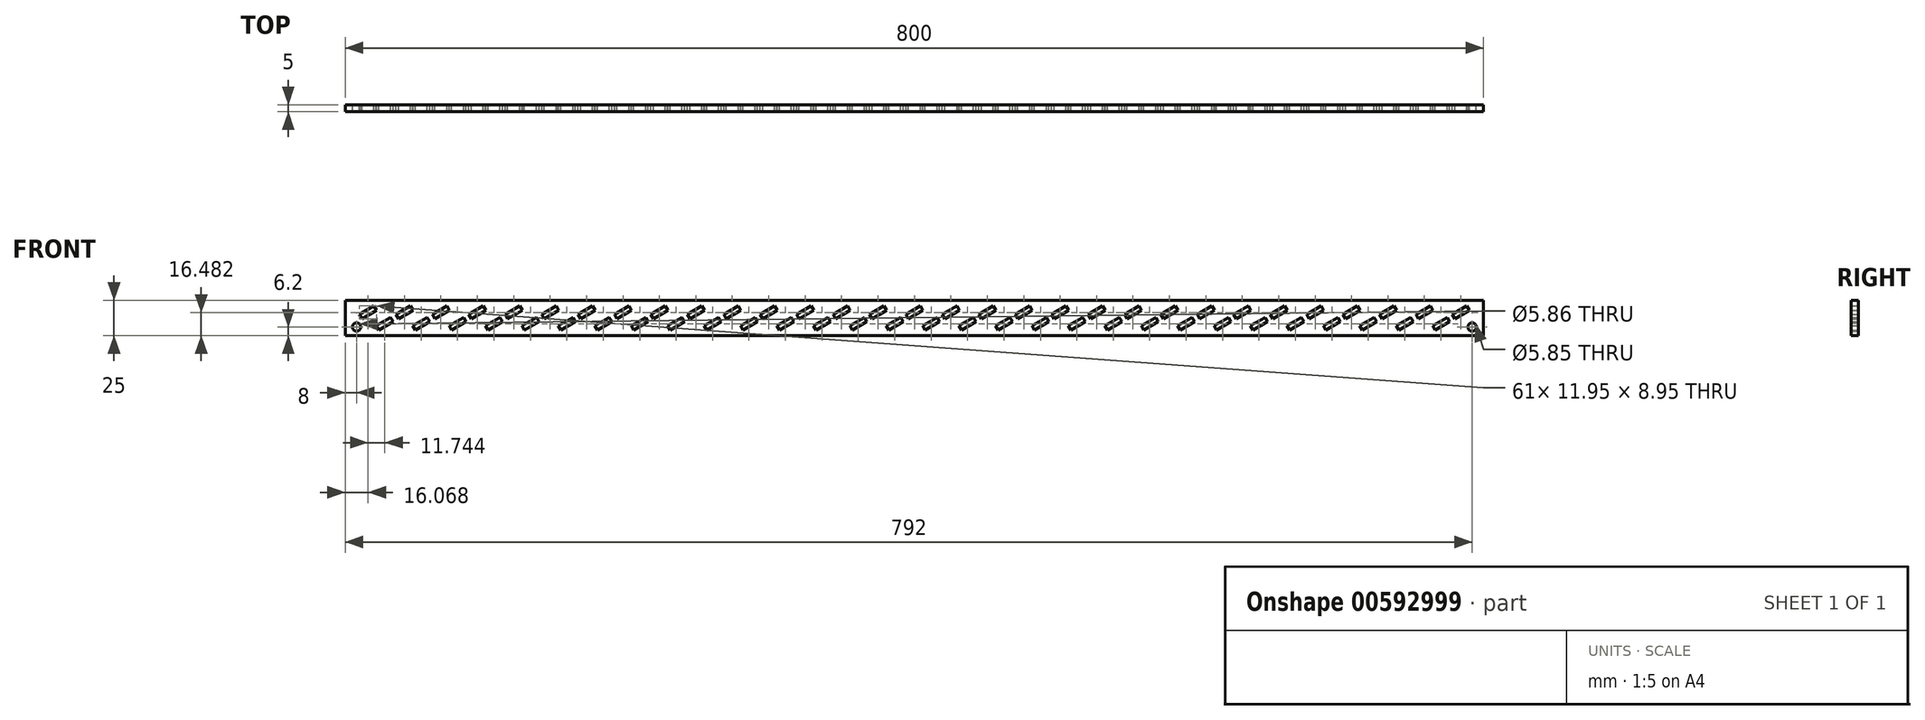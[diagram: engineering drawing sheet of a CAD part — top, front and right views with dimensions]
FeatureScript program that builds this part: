
annotation { "Feature Type Name" : "Feature", "Feature Type Description" : "" }
export const myFeature = defineFeature(function(context is Context, id is Id, definition is map)
    precondition{}
    {
        {
            var Q0;
            Q0=qCreatedBy(makeId("Front.planeOp"),FACE);
            var sketch = newSketch(context, id + "F0", { "sketchPlane" : qUnion([Q0])});
            skCircle(sketch, "E0", {"center": v(392, -6.3) * mm, "radius": 2.93 * mm});
            skCircle(sketch, "E1", {"center": v(192, 6.3) * mm, "radius": 2.93 * mm});
            skCircle(sketch, "E2", {"center": v(-1, -6.3) * mm, "radius": 2.93 * mm});
            skCircle(sketch, "E3", {"center": v(-216, 6.3) * mm, "radius": 2.93 * mm});
            skCircle(sketch, "E4", {"center": v(-392, -6.3) * mm, "radius": 2.93 * mm});
            skLineSegment(sketch, "E5", {"start": v(-382.04, 8.6) * mm, "end": v(-388.96, 4.6) * mm});
            skLineSegment(sketch, "E6", {"start": v(-385.96, -0.6) * mm, "end": v(-379.04, 3.4) * mm});
            skLineSegment(sketch, "E7", {"start": v(-370.3, 0.6) * mm, "end": v(-377.22, -3.4) * mm});
            skLineSegment(sketch, "E8", {"start": v(-374.22, -8.6) * mm, "end": v(-367.3, -4.6) * mm});
            skLineSegment(sketch, "E9", {"start": v(-356.44, 8.6) * mm, "end": v(-363.36, 4.6) * mm});
            skLineSegment(sketch, "E10", {"start": v(-360.36, -0.6) * mm, "end": v(-353.44, 3.4) * mm});
            skLineSegment(sketch, "E11", {"start": v(-344.7, 0.6) * mm, "end": v(-351.62, -3.4) * mm});
            skLineSegment(sketch, "E12", {"start": v(-348.62, -8.6) * mm, "end": v(-341.7, -4.6) * mm});
            skLineSegment(sketch, "E13", {"start": v(-330.84, 8.6) * mm, "end": v(-337.76, 4.6) * mm});
            skLineSegment(sketch, "E14", {"start": v(-334.76, -0.6) * mm, "end": v(-327.84, 3.4) * mm});
            skLineSegment(sketch, "E15", {"start": v(-319.1, 0.6) * mm, "end": v(-326.02, -3.4) * mm});
            skLineSegment(sketch, "E16", {"start": v(-323.02, -8.6) * mm, "end": v(-316.1, -4.6) * mm});
            skLineSegment(sketch, "E17", {"start": v(-305.24, 8.6) * mm, "end": v(-312.16, 4.6) * mm});
            skLineSegment(sketch, "E18", {"start": v(-309.16, -0.6) * mm, "end": v(-302.24, 3.4) * mm});
            skLineSegment(sketch, "E19", {"start": v(-293.5, 0.6) * mm, "end": v(-300.42, -3.4) * mm});
            skLineSegment(sketch, "E20", {"start": v(-297.42, -8.6) * mm, "end": v(-290.5, -4.6) * mm});
            skLineSegment(sketch, "E21", {"start": v(-279.64, 8.6) * mm, "end": v(-286.56, 4.6) * mm});
            skLineSegment(sketch, "E22", {"start": v(-283.56, -0.6) * mm, "end": v(-276.64, 3.4) * mm});
            skLineSegment(sketch, "E23", {"start": v(-267.9, 0.6) * mm, "end": v(-274.82, -3.4) * mm});
            skLineSegment(sketch, "E24", {"start": v(-271.82, -8.6) * mm, "end": v(-264.9, -4.6) * mm});
            skLineSegment(sketch, "E25", {"start": v(-254.04, 8.6) * mm, "end": v(-260.96, 4.6) * mm});
            skLineSegment(sketch, "E26", {"start": v(-257.96, -0.6) * mm, "end": v(-251.04, 3.4) * mm});
            skLineSegment(sketch, "E27", {"start": v(-242.3, 0.6) * mm, "end": v(-249.22, -3.4) * mm});
            skLineSegment(sketch, "E28", {"start": v(-246.22, -8.6) * mm, "end": v(-239.3, -4.6) * mm});
            skLineSegment(sketch, "E29", {"start": v(-228.44, 8.6) * mm, "end": v(-235.36, 4.6) * mm});
            skLineSegment(sketch, "E30", {"start": v(-232.36, -0.6) * mm, "end": v(-225.44, 3.4) * mm});
            skLineSegment(sketch, "E31", {"start": v(-216.7, 0.6) * mm, "end": v(-223.62, -3.4) * mm});
            skLineSegment(sketch, "E32", {"start": v(-220.62, -8.6) * mm, "end": v(-213.7, -4.6) * mm});
            skLineSegment(sketch, "E33", {"start": v(-202.84, 8.6) * mm, "end": v(-209.76, 4.6) * mm});
            skLineSegment(sketch, "E34", {"start": v(-206.76, -0.6) * mm, "end": v(-199.84, 3.4) * mm});
            skLineSegment(sketch, "E35", {"start": v(-191.1, 0.6) * mm, "end": v(-198.02, -3.4) * mm});
            skLineSegment(sketch, "E36", {"start": v(-195.02, -8.6) * mm, "end": v(-188.1, -4.6) * mm});
            skLineSegment(sketch, "E37", {"start": v(-177.24, 8.6) * mm, "end": v(-184.16, 4.6) * mm});
            skLineSegment(sketch, "E38", {"start": v(-181.16, -0.6) * mm, "end": v(-174.24, 3.4) * mm});
            skLineSegment(sketch, "E39", {"start": v(-165.5, 0.6) * mm, "end": v(-172.42, -3.4) * mm});
            skLineSegment(sketch, "E40", {"start": v(-169.42, -8.6) * mm, "end": v(-162.5, -4.6) * mm});
            skLineSegment(sketch, "E41", {"start": v(-151.64, 8.6) * mm, "end": v(-158.56, 4.6) * mm});
            skLineSegment(sketch, "E42", {"start": v(-155.56, -0.6) * mm, "end": v(-148.64, 3.4) * mm});
            skLineSegment(sketch, "E43", {"start": v(-139.9, 0.6) * mm, "end": v(-146.82, -3.4) * mm});
            skLineSegment(sketch, "E44", {"start": v(-143.82, -8.6) * mm, "end": v(-136.9, -4.6) * mm});
            skLineSegment(sketch, "E45", {"start": v(-126.04, 8.6) * mm, "end": v(-132.96, 4.6) * mm});
            skLineSegment(sketch, "E46", {"start": v(-129.96, -0.6) * mm, "end": v(-123.04, 3.4) * mm});
            skLineSegment(sketch, "E47", {"start": v(-114.3, 0.6) * mm, "end": v(-121.22, -3.4) * mm});
            skLineSegment(sketch, "E48", {"start": v(-118.22, -8.6) * mm, "end": v(-111.3, -4.6) * mm});
            skLineSegment(sketch, "E49", {"start": v(-100.44, 8.6) * mm, "end": v(-107.36, 4.6) * mm});
            skLineSegment(sketch, "E50", {"start": v(-104.36, -0.6) * mm, "end": v(-97.44, 3.4) * mm});
            skLineSegment(sketch, "E51", {"start": v(-88.7, 0.6) * mm, "end": v(-95.62, -3.4) * mm});
            skLineSegment(sketch, "E52", {"start": v(-92.62, -8.6) * mm, "end": v(-85.7, -4.6) * mm});
            skLineSegment(sketch, "E53", {"start": v(-74.84, 8.6) * mm, "end": v(-81.76, 4.6) * mm});
            skLineSegment(sketch, "E54", {"start": v(-78.76, -0.6) * mm, "end": v(-71.84, 3.4) * mm});
            skLineSegment(sketch, "E55", {"start": v(-63.1, 0.6) * mm, "end": v(-70.02, -3.4) * mm});
            skLineSegment(sketch, "E56", {"start": v(-67.02, -8.6) * mm, "end": v(-60.1, -4.6) * mm});
            skLineSegment(sketch, "E57", {"start": v(-49.24, 8.6) * mm, "end": v(-56.16, 4.6) * mm});
            skLineSegment(sketch, "E58", {"start": v(-53.16, -0.6) * mm, "end": v(-46.24, 3.4) * mm});
            skLineSegment(sketch, "E59", {"start": v(-37.5, 0.6) * mm, "end": v(-44.42, -3.4) * mm});
            skLineSegment(sketch, "E60", {"start": v(-41.42, -8.6) * mm, "end": v(-34.5, -4.6) * mm});
            skLineSegment(sketch, "E61", {"start": v(-23.64, 8.6) * mm, "end": v(-30.56, 4.6) * mm});
            skLineSegment(sketch, "E62", {"start": v(-27.56, -0.6) * mm, "end": v(-20.64, 3.4) * mm});
            skLineSegment(sketch, "E63", {"start": v(-11.9, 0.6) * mm, "end": v(-18.82, -3.4) * mm});
            skLineSegment(sketch, "E64", {"start": v(-15.82, -8.6) * mm, "end": v(-8.9, -4.6) * mm});
            skLineSegment(sketch, "E65", {"start": v(1.96, 8.6) * mm, "end": v(-4.96, 4.6) * mm});
            skLineSegment(sketch, "E66", {"start": v(-1.96, -0.6) * mm, "end": v(4.96, 3.4) * mm});
            skLineSegment(sketch, "E67", {"start": v(13.7, 0.6) * mm, "end": v(6.78, -3.4) * mm});
            skLineSegment(sketch, "E68", {"start": v(9.78, -8.6) * mm, "end": v(16.7, -4.6) * mm});
            skLineSegment(sketch, "E69", {"start": v(27.56, 8.6) * mm, "end": v(20.64, 4.6) * mm});
            skLineSegment(sketch, "E70", {"start": v(23.64, -0.6) * mm, "end": v(30.56, 3.4) * mm});
            skLineSegment(sketch, "E71", {"start": v(39.3, 0.6) * mm, "end": v(32.38, -3.4) * mm});
            skLineSegment(sketch, "E72", {"start": v(35.38, -8.6) * mm, "end": v(42.3, -4.6) * mm});
            skLineSegment(sketch, "E73", {"start": v(53.16, 8.6) * mm, "end": v(46.24, 4.6) * mm});
            skLineSegment(sketch, "E74", {"start": v(49.24, -0.6) * mm, "end": v(56.16, 3.4) * mm});
            skLineSegment(sketch, "E75", {"start": v(64.9, 0.6) * mm, "end": v(57.98, -3.4) * mm});
            skLineSegment(sketch, "E76", {"start": v(60.98, -8.6) * mm, "end": v(67.9, -4.6) * mm});
            skLineSegment(sketch, "E77", {"start": v(78.76, 8.6) * mm, "end": v(71.84, 4.6) * mm});
            skLineSegment(sketch, "E78", {"start": v(74.84, -0.6) * mm, "end": v(81.76, 3.4) * mm});
            skLineSegment(sketch, "E79", {"start": v(90.5, 0.6) * mm, "end": v(83.58, -3.4) * mm});
            skLineSegment(sketch, "E80", {"start": v(86.58, -8.6) * mm, "end": v(93.5, -4.6) * mm});
            skLineSegment(sketch, "E81", {"start": v(104.36, 8.6) * mm, "end": v(97.44, 4.6) * mm});
            skLineSegment(sketch, "E82", {"start": v(100.44, -0.6) * mm, "end": v(107.36, 3.4) * mm});
            skLineSegment(sketch, "E83", {"start": v(116.1, 0.6) * mm, "end": v(109.18, -3.4) * mm});
            skLineSegment(sketch, "E84", {"start": v(112.18, -8.6) * mm, "end": v(119.1, -4.6) * mm});
            skLineSegment(sketch, "E85", {"start": v(129.96, 8.6) * mm, "end": v(123.04, 4.6) * mm});
            skLineSegment(sketch, "E86", {"start": v(126.04, -0.6) * mm, "end": v(132.96, 3.4) * mm});
            skLineSegment(sketch, "E87", {"start": v(141.7, 0.6) * mm, "end": v(134.78, -3.4) * mm});
            skLineSegment(sketch, "E88", {"start": v(137.78, -8.6) * mm, "end": v(144.7, -4.6) * mm});
            skLineSegment(sketch, "E89", {"start": v(155.56, 8.6) * mm, "end": v(148.64, 4.6) * mm});
            skLineSegment(sketch, "E90", {"start": v(151.64, -0.6) * mm, "end": v(158.56, 3.4) * mm});
            skLineSegment(sketch, "E91", {"start": v(167.3, 0.6) * mm, "end": v(160.38, -3.4) * mm});
            skLineSegment(sketch, "E92", {"start": v(163.38, -8.6) * mm, "end": v(170.3, -4.6) * mm});
            skLineSegment(sketch, "E93", {"start": v(181.16, 8.6) * mm, "end": v(174.24, 4.6) * mm});
            skLineSegment(sketch, "E94", {"start": v(177.24, -0.6) * mm, "end": v(184.16, 3.4) * mm});
            skLineSegment(sketch, "E95", {"start": v(192.9, 0.6) * mm, "end": v(185.98, -3.4) * mm});
            skLineSegment(sketch, "E96", {"start": v(188.98, -8.6) * mm, "end": v(195.9, -4.6) * mm});
            skLineSegment(sketch, "E97", {"start": v(206.76, 8.6) * mm, "end": v(199.84, 4.6) * mm});
            skLineSegment(sketch, "E98", {"start": v(202.84, -0.6) * mm, "end": v(209.76, 3.4) * mm});
            skLineSegment(sketch, "E99", {"start": v(218.5, 0.6) * mm, "end": v(211.58, -3.4) * mm});
            skLineSegment(sketch, "E100", {"start": v(214.58, -8.6) * mm, "end": v(221.5, -4.6) * mm});
            skLineSegment(sketch, "E101", {"start": v(232.36, 8.6) * mm, "end": v(225.44, 4.6) * mm});
            skLineSegment(sketch, "E102", {"start": v(228.44, -0.6) * mm, "end": v(235.36, 3.4) * mm});
            skLineSegment(sketch, "E103", {"start": v(244.1, 0.6) * mm, "end": v(237.18, -3.4) * mm});
            skLineSegment(sketch, "E104", {"start": v(240.18, -8.6) * mm, "end": v(247.1, -4.6) * mm});
            skLineSegment(sketch, "E105", {"start": v(257.96, 8.6) * mm, "end": v(251.04, 4.6) * mm});
            skLineSegment(sketch, "E106", {"start": v(254.04, -0.6) * mm, "end": v(260.96, 3.4) * mm});
            skLineSegment(sketch, "E107", {"start": v(269.7, 0.6) * mm, "end": v(262.78, -3.4) * mm});
            skLineSegment(sketch, "E108", {"start": v(265.78, -8.6) * mm, "end": v(272.7, -4.6) * mm});
            skLineSegment(sketch, "E109", {"start": v(283.56, 8.6) * mm, "end": v(276.64, 4.6) * mm});
            skLineSegment(sketch, "E110", {"start": v(279.64, -0.6) * mm, "end": v(286.56, 3.4) * mm});
            skLineSegment(sketch, "E111", {"start": v(295.3, 0.6) * mm, "end": v(288.38, -3.4) * mm});
            skLineSegment(sketch, "E112", {"start": v(291.38, -8.6) * mm, "end": v(298.3, -4.6) * mm});
            skLineSegment(sketch, "E113", {"start": v(309.16, 8.6) * mm, "end": v(302.24, 4.6) * mm});
            skLineSegment(sketch, "E114", {"start": v(305.24, -0.6) * mm, "end": v(312.16, 3.4) * mm});
            skLineSegment(sketch, "E115", {"start": v(320.9, 0.6) * mm, "end": v(313.98, -3.4) * mm});
            skLineSegment(sketch, "E116", {"start": v(316.98, -8.6) * mm, "end": v(323.9, -4.6) * mm});
            skLineSegment(sketch, "E117", {"start": v(334.76, 8.6) * mm, "end": v(327.84, 4.6) * mm});
            skLineSegment(sketch, "E118", {"start": v(330.84, -0.6) * mm, "end": v(337.76, 3.4) * mm});
            skLineSegment(sketch, "E119", {"start": v(346.5, 0.6) * mm, "end": v(339.58, -3.4) * mm});
            skLineSegment(sketch, "E120", {"start": v(342.58, -8.6) * mm, "end": v(349.5, -4.6) * mm});
            skLineSegment(sketch, "E121", {"start": v(360.36, 8.6) * mm, "end": v(353.44, 4.6) * mm});
            skLineSegment(sketch, "E122", {"start": v(356.44, -0.6) * mm, "end": v(363.36, 3.4) * mm});
            skLineSegment(sketch, "E123", {"start": v(372.1, 0.6) * mm, "end": v(365.18, -3.4) * mm});
            skLineSegment(sketch, "E124", {"start": v(368.18, -8.6) * mm, "end": v(375.1, -4.6) * mm});
            skLineSegment(sketch, "E125", {"start": v(385.96, 8.6) * mm, "end": v(379.04, 4.6) * mm});
            skLineSegment(sketch, "E126", {"start": v(382.04, -0.6) * mm, "end": v(388.96, 3.4) * mm});
            skLineSegment(sketch, "E127", {"start": v(400, 12.5) * mm, "end": v(-400, 12.5) * mm});
            skLineSegment(sketch, "E128", {"start": v(400, -12.5) * mm, "end": v(400, 12.5) * mm});
            skLineSegment(sketch, "E129", {"start": v(-400, -12.5) * mm, "end": v(400, -12.5) * mm});
            skLineSegment(sketch, "E130", {"start": v(-400, 12.5) * mm, "end": v(-400, -12.5) * mm});
            skArc(sketch, "E131", {"start": v(-379.04, 3.4) * mm, "mid": v(-377.94, 7.5) * mm, "end": v(-382.04, 8.6) * mm});
            skArc(sketch, "E132", {"start": v(-388.96, 4.6) * mm, "mid": v(-390.06, 0.5) * mm, "end": v(-385.96, -0.6) * mm});
            skArc(sketch, "E133", {"start": v(-367.3, -4.6) * mm, "mid": v(-366.2, -0.5) * mm, "end": v(-370.3, 0.6) * mm});
            skArc(sketch, "E134", {"start": v(-377.22, -3.4) * mm, "mid": v(-378.32, -7.5) * mm, "end": v(-374.22, -8.6) * mm});
            skArc(sketch, "E135", {"start": v(-353.44, 3.4) * mm, "mid": v(-352.34, 7.5) * mm, "end": v(-356.44, 8.6) * mm});
            skArc(sketch, "E136", {"start": v(-363.36, 4.6) * mm, "mid": v(-364.46, 0.5) * mm, "end": v(-360.36, -0.6) * mm});
            skArc(sketch, "E137", {"start": v(-341.7, -4.6) * mm, "mid": v(-340.6, -0.5) * mm, "end": v(-344.7, 0.6) * mm});
            skArc(sketch, "E138", {"start": v(-351.62, -3.4) * mm, "mid": v(-352.72, -7.5) * mm, "end": v(-348.62, -8.6) * mm});
            skArc(sketch, "E139", {"start": v(-327.84, 3.4) * mm, "mid": v(-326.74, 7.5) * mm, "end": v(-330.84, 8.6) * mm});
            skArc(sketch, "E140", {"start": v(-337.76, 4.6) * mm, "mid": v(-338.86, 0.5) * mm, "end": v(-334.76, -0.6) * mm});
            skArc(sketch, "E141", {"start": v(-316.1, -4.6) * mm, "mid": v(-315, -0.5) * mm, "end": v(-319.1, 0.6) * mm});
            skArc(sketch, "E142", {"start": v(-326.02, -3.4) * mm, "mid": v(-327.12, -7.5) * mm, "end": v(-323.02, -8.6) * mm});
            skArc(sketch, "E143", {"start": v(-302.24, 3.4) * mm, "mid": v(-301.14, 7.5) * mm, "end": v(-305.24, 8.6) * mm});
            skArc(sketch, "E144", {"start": v(-312.16, 4.6) * mm, "mid": v(-313.26, 0.5) * mm, "end": v(-309.16, -0.6) * mm});
            skArc(sketch, "E145", {"start": v(-290.5, -4.6) * mm, "mid": v(-289.4, -0.5) * mm, "end": v(-293.5, 0.6) * mm});
            skArc(sketch, "E146", {"start": v(-300.42, -3.4) * mm, "mid": v(-301.52, -7.5) * mm, "end": v(-297.42, -8.6) * mm});
            skArc(sketch, "E147", {"start": v(-276.64, 3.4) * mm, "mid": v(-275.54, 7.5) * mm, "end": v(-279.64, 8.6) * mm});
            skArc(sketch, "E148", {"start": v(-286.56, 4.6) * mm, "mid": v(-287.66, 0.5) * mm, "end": v(-283.56, -0.6) * mm});
            skArc(sketch, "E149", {"start": v(-264.9, -4.6) * mm, "mid": v(-263.8, -0.5) * mm, "end": v(-267.9, 0.6) * mm});
            skArc(sketch, "E150", {"start": v(-274.82, -3.4) * mm, "mid": v(-275.92, -7.5) * mm, "end": v(-271.82, -8.6) * mm});
            skArc(sketch, "E151", {"start": v(-251.04, 3.4) * mm, "mid": v(-249.94, 7.5) * mm, "end": v(-254.04, 8.6) * mm});
            skArc(sketch, "E152", {"start": v(-260.96, 4.6) * mm, "mid": v(-262.06, 0.5) * mm, "end": v(-257.96, -0.6) * mm});
            skArc(sketch, "E153", {"start": v(-239.3, -4.6) * mm, "mid": v(-238.2, -0.5) * mm, "end": v(-242.3, 0.6) * mm});
            skArc(sketch, "E154", {"start": v(-249.22, -3.4) * mm, "mid": v(-250.32, -7.5) * mm, "end": v(-246.22, -8.6) * mm});
            skArc(sketch, "E155", {"start": v(-225.44, 3.4) * mm, "mid": v(-224.34, 7.5) * mm, "end": v(-228.44, 8.6) * mm});
            skArc(sketch, "E156", {"start": v(-235.36, 4.6) * mm, "mid": v(-236.46, 0.5) * mm, "end": v(-232.36, -0.6) * mm});
            skArc(sketch, "E157", {"start": v(-213.7, -4.6) * mm, "mid": v(-212.6, -0.5) * mm, "end": v(-216.7, 0.6) * mm});
            skArc(sketch, "E158", {"start": v(-223.62, -3.4) * mm, "mid": v(-224.72, -7.5) * mm, "end": v(-220.62, -8.6) * mm});
            skArc(sketch, "E159", {"start": v(-199.84, 3.4) * mm, "mid": v(-198.74, 7.5) * mm, "end": v(-202.84, 8.6) * mm});
            skArc(sketch, "E160", {"start": v(-209.76, 4.6) * mm, "mid": v(-210.86, 0.5) * mm, "end": v(-206.76, -0.6) * mm});
            skArc(sketch, "E161", {"start": v(-188.1, -4.6) * mm, "mid": v(-187, -0.5) * mm, "end": v(-191.1, 0.6) * mm});
            skArc(sketch, "E162", {"start": v(-198.02, -3.4) * mm, "mid": v(-199.12, -7.5) * mm, "end": v(-195.02, -8.6) * mm});
            skArc(sketch, "E163", {"start": v(-174.24, 3.4) * mm, "mid": v(-173.14, 7.5) * mm, "end": v(-177.24, 8.6) * mm});
            skArc(sketch, "E164", {"start": v(-184.16, 4.6) * mm, "mid": v(-185.26, 0.5) * mm, "end": v(-181.16, -0.6) * mm});
            skArc(sketch, "E165", {"start": v(-162.5, -4.6) * mm, "mid": v(-161.4, -0.5) * mm, "end": v(-165.5, 0.6) * mm});
            skArc(sketch, "E166", {"start": v(-172.42, -3.4) * mm, "mid": v(-173.52, -7.5) * mm, "end": v(-169.42, -8.6) * mm});
            skArc(sketch, "E167", {"start": v(-148.64, 3.4) * mm, "mid": v(-147.54, 7.5) * mm, "end": v(-151.64, 8.6) * mm});
            skArc(sketch, "E168", {"start": v(-158.56, 4.6) * mm, "mid": v(-159.66, 0.5) * mm, "end": v(-155.56, -0.6) * mm});
            skArc(sketch, "E169", {"start": v(-136.9, -4.6) * mm, "mid": v(-135.8, -0.5) * mm, "end": v(-139.9, 0.6) * mm});
            skArc(sketch, "E170", {"start": v(-146.82, -3.4) * mm, "mid": v(-147.92, -7.5) * mm, "end": v(-143.82, -8.6) * mm});
            skArc(sketch, "E171", {"start": v(-123.04, 3.4) * mm, "mid": v(-121.94, 7.5) * mm, "end": v(-126.04, 8.6) * mm});
            skArc(sketch, "E172", {"start": v(-132.96, 4.6) * mm, "mid": v(-134.06, 0.5) * mm, "end": v(-129.96, -0.6) * mm});
            skArc(sketch, "E173", {"start": v(-111.3, -4.6) * mm, "mid": v(-110.2, -0.5) * mm, "end": v(-114.3, 0.6) * mm});
            skArc(sketch, "E174", {"start": v(-121.22, -3.4) * mm, "mid": v(-122.32, -7.5) * mm, "end": v(-118.22, -8.6) * mm});
            skArc(sketch, "E175", {"start": v(-97.44, 3.4) * mm, "mid": v(-96.34, 7.5) * mm, "end": v(-100.44, 8.6) * mm});
            skArc(sketch, "E176", {"start": v(-107.36, 4.6) * mm, "mid": v(-108.46, 0.5) * mm, "end": v(-104.36, -0.6) * mm});
            skArc(sketch, "E177", {"start": v(-85.7, -4.6) * mm, "mid": v(-84.6, -0.5) * mm, "end": v(-88.7, 0.6) * mm});
            skArc(sketch, "E178", {"start": v(-95.62, -3.4) * mm, "mid": v(-96.72, -7.5) * mm, "end": v(-92.62, -8.6) * mm});
            skArc(sketch, "E179", {"start": v(-71.84, 3.4) * mm, "mid": v(-70.74, 7.5) * mm, "end": v(-74.84, 8.6) * mm});
            skArc(sketch, "E180", {"start": v(-81.76, 4.6) * mm, "mid": v(-82.86, 0.5) * mm, "end": v(-78.76, -0.6) * mm});
            skArc(sketch, "E181", {"start": v(-60.1, -4.6) * mm, "mid": v(-59, -0.5) * mm, "end": v(-63.1, 0.6) * mm});
            skArc(sketch, "E182", {"start": v(-70.02, -3.4) * mm, "mid": v(-71.12, -7.5) * mm, "end": v(-67.02, -8.6) * mm});
            skArc(sketch, "E183", {"start": v(-46.24, 3.4) * mm, "mid": v(-45.14, 7.5) * mm, "end": v(-49.24, 8.6) * mm});
            skArc(sketch, "E184", {"start": v(-56.16, 4.6) * mm, "mid": v(-57.26, 0.5) * mm, "end": v(-53.16, -0.6) * mm});
            skArc(sketch, "E185", {"start": v(-34.5, -4.6) * mm, "mid": v(-33.4, -0.5) * mm, "end": v(-37.5, 0.6) * mm});
            skArc(sketch, "E186", {"start": v(-44.42, -3.4) * mm, "mid": v(-45.52, -7.5) * mm, "end": v(-41.42, -8.6) * mm});
            skArc(sketch, "E187", {"start": v(-20.64, 3.4) * mm, "mid": v(-19.54, 7.5) * mm, "end": v(-23.64, 8.6) * mm});
            skArc(sketch, "E188", {"start": v(-30.56, 4.6) * mm, "mid": v(-31.66, 0.5) * mm, "end": v(-27.56, -0.6) * mm});
            skArc(sketch, "E189", {"start": v(-8.9, -4.6) * mm, "mid": v(-7.8, -0.5) * mm, "end": v(-11.9, 0.6) * mm});
            skArc(sketch, "E190", {"start": v(-18.82, -3.4) * mm, "mid": v(-19.92, -7.5) * mm, "end": v(-15.82, -8.6) * mm});
            skArc(sketch, "E191", {"start": v(4.96, 3.4) * mm, "mid": v(6.06, 7.5) * mm, "end": v(1.96, 8.6) * mm});
            skArc(sketch, "E192", {"start": v(-4.96, 4.6) * mm, "mid": v(-6.06, 0.5) * mm, "end": v(-1.96, -0.6) * mm});
            skArc(sketch, "E193", {"start": v(16.7, -4.6) * mm, "mid": v(17.8, -0.5) * mm, "end": v(13.7, 0.6) * mm});
            skArc(sketch, "E194", {"start": v(6.78, -3.4) * mm, "mid": v(5.68, -7.5) * mm, "end": v(9.78, -8.6) * mm});
            skArc(sketch, "E195", {"start": v(30.56, 3.4) * mm, "mid": v(31.66, 7.5) * mm, "end": v(27.56, 8.6) * mm});
            skArc(sketch, "E196", {"start": v(20.64, 4.6) * mm, "mid": v(19.54, 0.5) * mm, "end": v(23.64, -0.6) * mm});
            skArc(sketch, "E197", {"start": v(42.3, -4.6) * mm, "mid": v(43.4, -0.5) * mm, "end": v(39.3, 0.6) * mm});
            skArc(sketch, "E198", {"start": v(32.38, -3.4) * mm, "mid": v(31.28, -7.5) * mm, "end": v(35.38, -8.6) * mm});
            skArc(sketch, "E199", {"start": v(56.16, 3.4) * mm, "mid": v(57.26, 7.5) * mm, "end": v(53.16, 8.6) * mm});
            skArc(sketch, "E200", {"start": v(46.24, 4.6) * mm, "mid": v(45.14, 0.5) * mm, "end": v(49.24, -0.6) * mm});
            skArc(sketch, "E201", {"start": v(67.9, -4.6) * mm, "mid": v(69, -0.5) * mm, "end": v(64.9, 0.6) * mm});
            skArc(sketch, "E202", {"start": v(57.98, -3.4) * mm, "mid": v(56.88, -7.5) * mm, "end": v(60.98, -8.6) * mm});
            skArc(sketch, "E203", {"start": v(81.76, 3.4) * mm, "mid": v(82.86, 7.5) * mm, "end": v(78.76, 8.6) * mm});
            skArc(sketch, "E204", {"start": v(71.84, 4.6) * mm, "mid": v(70.74, 0.5) * mm, "end": v(74.84, -0.6) * mm});
            skArc(sketch, "E205", {"start": v(93.5, -4.6) * mm, "mid": v(94.6, -0.5) * mm, "end": v(90.5, 0.6) * mm});
            skArc(sketch, "E206", {"start": v(83.58, -3.4) * mm, "mid": v(82.48, -7.5) * mm, "end": v(86.58, -8.6) * mm});
            skArc(sketch, "E207", {"start": v(107.36, 3.4) * mm, "mid": v(108.46, 7.5) * mm, "end": v(104.36, 8.6) * mm});
            skArc(sketch, "E208", {"start": v(97.44, 4.6) * mm, "mid": v(96.34, 0.5) * mm, "end": v(100.44, -0.6) * mm});
            skArc(sketch, "E209", {"start": v(119.1, -4.6) * mm, "mid": v(120.2, -0.5) * mm, "end": v(116.1, 0.6) * mm});
            skArc(sketch, "E210", {"start": v(109.18, -3.4) * mm, "mid": v(108.08, -7.5) * mm, "end": v(112.18, -8.6) * mm});
            skArc(sketch, "E211", {"start": v(132.96, 3.4) * mm, "mid": v(134.06, 7.5) * mm, "end": v(129.96, 8.6) * mm});
            skArc(sketch, "E212", {"start": v(123.04, 4.6) * mm, "mid": v(121.94, 0.5) * mm, "end": v(126.04, -0.6) * mm});
            skArc(sketch, "E213", {"start": v(144.7, -4.6) * mm, "mid": v(145.8, -0.5) * mm, "end": v(141.7, 0.6) * mm});
            skArc(sketch, "E214", {"start": v(134.78, -3.4) * mm, "mid": v(133.68, -7.5) * mm, "end": v(137.78, -8.6) * mm});
            skArc(sketch, "E215", {"start": v(158.56, 3.4) * mm, "mid": v(159.66, 7.5) * mm, "end": v(155.56, 8.6) * mm});
            skArc(sketch, "E216", {"start": v(148.64, 4.6) * mm, "mid": v(147.54, 0.5) * mm, "end": v(151.64, -0.6) * mm});
            skArc(sketch, "E217", {"start": v(170.3, -4.6) * mm, "mid": v(171.4, -0.5) * mm, "end": v(167.3, 0.6) * mm});
            skArc(sketch, "E218", {"start": v(160.38, -3.4) * mm, "mid": v(159.28, -7.5) * mm, "end": v(163.38, -8.6) * mm});
            skArc(sketch, "E219", {"start": v(184.16, 3.4) * mm, "mid": v(185.26, 7.5) * mm, "end": v(181.16, 8.6) * mm});
            skArc(sketch, "E220", {"start": v(174.24, 4.6) * mm, "mid": v(173.14, 0.5) * mm, "end": v(177.24, -0.6) * mm});
            skArc(sketch, "E221", {"start": v(195.9, -4.6) * mm, "mid": v(197, -0.5) * mm, "end": v(192.9, 0.6) * mm});
            skArc(sketch, "E222", {"start": v(185.98, -3.4) * mm, "mid": v(184.88, -7.5) * mm, "end": v(188.98, -8.6) * mm});
            skArc(sketch, "E223", {"start": v(209.76, 3.4) * mm, "mid": v(210.86, 7.5) * mm, "end": v(206.76, 8.6) * mm});
            skArc(sketch, "E224", {"start": v(199.84, 4.6) * mm, "mid": v(198.74, 0.5) * mm, "end": v(202.84, -0.6) * mm});
            skArc(sketch, "E225", {"start": v(221.5, -4.6) * mm, "mid": v(222.6, -0.5) * mm, "end": v(218.5, 0.6) * mm});
            skArc(sketch, "E226", {"start": v(211.58, -3.4) * mm, "mid": v(210.48, -7.5) * mm, "end": v(214.58, -8.6) * mm});
            skArc(sketch, "E227", {"start": v(235.36, 3.4) * mm, "mid": v(236.46, 7.5) * mm, "end": v(232.36, 8.6) * mm});
            skArc(sketch, "E228", {"start": v(225.44, 4.6) * mm, "mid": v(224.34, 0.5) * mm, "end": v(228.44, -0.6) * mm});
            skArc(sketch, "E229", {"start": v(247.1, -4.6) * mm, "mid": v(248.2, -0.5) * mm, "end": v(244.1, 0.6) * mm});
            skArc(sketch, "E230", {"start": v(237.18, -3.4) * mm, "mid": v(236.08, -7.5) * mm, "end": v(240.18, -8.6) * mm});
            skArc(sketch, "E231", {"start": v(260.96, 3.4) * mm, "mid": v(262.06, 7.5) * mm, "end": v(257.96, 8.6) * mm});
            skArc(sketch, "E232", {"start": v(251.04, 4.6) * mm, "mid": v(249.94, 0.5) * mm, "end": v(254.04, -0.6) * mm});
            skArc(sketch, "E233", {"start": v(272.7, -4.6) * mm, "mid": v(273.8, -0.5) * mm, "end": v(269.7, 0.6) * mm});
            skArc(sketch, "E234", {"start": v(262.78, -3.4) * mm, "mid": v(261.68, -7.5) * mm, "end": v(265.78, -8.6) * mm});
            skArc(sketch, "E235", {"start": v(286.56, 3.4) * mm, "mid": v(287.66, 7.5) * mm, "end": v(283.56, 8.6) * mm});
            skArc(sketch, "E236", {"start": v(276.64, 4.6) * mm, "mid": v(275.54, 0.5) * mm, "end": v(279.64, -0.6) * mm});
            skArc(sketch, "E237", {"start": v(298.3, -4.6) * mm, "mid": v(299.4, -0.5) * mm, "end": v(295.3, 0.6) * mm});
            skArc(sketch, "E238", {"start": v(288.38, -3.4) * mm, "mid": v(287.28, -7.5) * mm, "end": v(291.38, -8.6) * mm});
            skArc(sketch, "E239", {"start": v(312.16, 3.4) * mm, "mid": v(313.26, 7.5) * mm, "end": v(309.16, 8.6) * mm});
            skArc(sketch, "E240", {"start": v(302.24, 4.6) * mm, "mid": v(301.14, 0.5) * mm, "end": v(305.24, -0.6) * mm});
            skArc(sketch, "E241", {"start": v(323.9, -4.6) * mm, "mid": v(325, -0.5) * mm, "end": v(320.9, 0.6) * mm});
            skArc(sketch, "E242", {"start": v(313.98, -3.4) * mm, "mid": v(312.88, -7.5) * mm, "end": v(316.98, -8.6) * mm});
            skArc(sketch, "E243", {"start": v(337.76, 3.4) * mm, "mid": v(338.86, 7.5) * mm, "end": v(334.76, 8.6) * mm});
            skArc(sketch, "E244", {"start": v(327.84, 4.6) * mm, "mid": v(326.74, 0.5) * mm, "end": v(330.84, -0.6) * mm});
            skArc(sketch, "E245", {"start": v(349.5, -4.6) * mm, "mid": v(350.6, -0.5) * mm, "end": v(346.5, 0.6) * mm});
            skArc(sketch, "E246", {"start": v(339.58, -3.4) * mm, "mid": v(338.48, -7.5) * mm, "end": v(342.58, -8.6) * mm});
            skArc(sketch, "E247", {"start": v(363.36, 3.4) * mm, "mid": v(364.46, 7.5) * mm, "end": v(360.36, 8.6) * mm});
            skArc(sketch, "E248", {"start": v(353.44, 4.6) * mm, "mid": v(352.34, 0.5) * mm, "end": v(356.44, -0.6) * mm});
            skArc(sketch, "E249", {"start": v(375.1, -4.6) * mm, "mid": v(376.2, -0.5) * mm, "end": v(372.1, 0.6) * mm});
            skArc(sketch, "E250", {"start": v(365.18, -3.4) * mm, "mid": v(364.08, -7.5) * mm, "end": v(368.18, -8.6) * mm});
            skArc(sketch, "E251", {"start": v(388.96, 3.4) * mm, "mid": v(390.06, 7.5) * mm, "end": v(385.96, 8.6) * mm});
            skArc(sketch, "E252", {"start": v(379.04, 4.6) * mm, "mid": v(377.94, 0.5) * mm, "end": v(382.04, -0.6) * mm});
            skSolve(sketch);
        }
        {
            var Q0;
            Q0=qCreatedBy(makeId("Front.planeOp"),FACE);
            var sketch = newSketch(context, id + "F1", { "sketchPlane" : qUnion([Q0])});
            skLineSegment(sketch, "E253", {"start": v(390.04, 5.38) * mm, "end": v(388.27, 8.46) * mm});
            skLineSegment(sketch, "E254", {"start": v(388.27, 8.46) * mm, "end": v(378.1, 2.58) * mm});
            skLineSegment(sketch, "E255", {"start": v(378.1, 2.58) * mm, "end": v(379.87, -0.5) * mm});
            skLineSegment(sketch, "E256", {"start": v(379.87, -0.5) * mm, "end": v(390.04, 5.38) * mm});
            skLineSegment(sketch, "E257", {"start": v(374.41, 0.46) * mm, "end": v(376.19, -2.62) * mm});
            skLineSegment(sketch, "E258", {"start": v(376.19, -2.62) * mm, "end": v(366.01, -8.5) * mm});
            skLineSegment(sketch, "E259", {"start": v(366.01, -8.5) * mm, "end": v(364.24, -5.42) * mm});
            skLineSegment(sketch, "E260", {"start": v(364.24, -5.42) * mm, "end": v(374.41, 0.46) * mm});
            skLineSegment(sketch, "E261.1.0.0", {"start": v(362.67, 8.46) * mm, "end": v(352.5, 2.58) * mm});
            skLineSegment(sketch, "E261.1.0.1", {"start": v(364.44, 5.38) * mm, "end": v(362.67, 8.46) * mm});
            skLineSegment(sketch, "E261.1.0.2", {"start": v(354.27, -0.5) * mm, "end": v(364.44, 5.38) * mm});
            skLineSegment(sketch, "E261.1.0.3", {"start": v(352.5, 2.58) * mm, "end": v(354.27, -0.5) * mm});
            skLineSegment(sketch, "E261.1.0.4", {"start": v(348.81, 0.46) * mm, "end": v(350.59, -2.62) * mm});
            skLineSegment(sketch, "E261.1.0.5", {"start": v(338.64, -5.42) * mm, "end": v(348.81, 0.46) * mm});
            skLineSegment(sketch, "E261.1.0.6", {"start": v(350.59, -2.62) * mm, "end": v(340.41, -8.5) * mm});
            skLineSegment(sketch, "E261.1.0.7", {"start": v(340.41, -8.5) * mm, "end": v(338.64, -5.42) * mm});
            skLineSegment(sketch, "E261.2.0.0", {"start": v(337.07, 8.46) * mm, "end": v(326.9, 2.58) * mm});
            skLineSegment(sketch, "E261.2.0.1", {"start": v(338.84, 5.38) * mm, "end": v(337.07, 8.46) * mm});
            skLineSegment(sketch, "E261.2.0.2", {"start": v(328.67, -0.5) * mm, "end": v(338.84, 5.38) * mm});
            skLineSegment(sketch, "E261.2.0.3", {"start": v(326.9, 2.58) * mm, "end": v(328.67, -0.5) * mm});
            skLineSegment(sketch, "E261.2.0.4", {"start": v(323.21, 0.46) * mm, "end": v(324.99, -2.62) * mm});
            skLineSegment(sketch, "E261.2.0.5", {"start": v(313.04, -5.42) * mm, "end": v(323.21, 0.46) * mm});
            skLineSegment(sketch, "E261.2.0.6", {"start": v(324.99, -2.62) * mm, "end": v(314.81, -8.5) * mm});
            skLineSegment(sketch, "E261.2.0.7", {"start": v(314.81, -8.5) * mm, "end": v(313.04, -5.42) * mm});
            skLineSegment(sketch, "E261.3.0.0", {"start": v(311.47, 8.46) * mm, "end": v(301.3, 2.58) * mm});
            skLineSegment(sketch, "E261.3.0.1", {"start": v(313.24, 5.38) * mm, "end": v(311.47, 8.46) * mm});
            skLineSegment(sketch, "E261.3.0.2", {"start": v(303.07, -0.5) * mm, "end": v(313.24, 5.38) * mm});
            skLineSegment(sketch, "E261.3.0.3", {"start": v(301.3, 2.58) * mm, "end": v(303.07, -0.5) * mm});
            skLineSegment(sketch, "E261.3.0.4", {"start": v(297.61, 0.46) * mm, "end": v(299.39, -2.62) * mm});
            skLineSegment(sketch, "E261.3.0.5", {"start": v(287.44, -5.42) * mm, "end": v(297.61, 0.46) * mm});
            skLineSegment(sketch, "E261.3.0.6", {"start": v(299.39, -2.62) * mm, "end": v(289.21, -8.5) * mm});
            skLineSegment(sketch, "E261.3.0.7", {"start": v(289.21, -8.5) * mm, "end": v(287.44, -5.42) * mm});
            skLineSegment(sketch, "E261.4.0.0", {"start": v(285.87, 8.46) * mm, "end": v(275.7, 2.58) * mm});
            skLineSegment(sketch, "E261.4.0.1", {"start": v(287.64, 5.38) * mm, "end": v(285.87, 8.46) * mm});
            skLineSegment(sketch, "E261.4.0.2", {"start": v(277.47, -0.5) * mm, "end": v(287.64, 5.38) * mm});
            skLineSegment(sketch, "E261.4.0.3", {"start": v(275.7, 2.58) * mm, "end": v(277.47, -0.5) * mm});
            skLineSegment(sketch, "E261.4.0.4", {"start": v(272.01, 0.46) * mm, "end": v(273.79, -2.62) * mm});
            skLineSegment(sketch, "E261.4.0.5", {"start": v(261.84, -5.42) * mm, "end": v(272.01, 0.46) * mm});
            skLineSegment(sketch, "E261.4.0.6", {"start": v(273.79, -2.62) * mm, "end": v(263.61, -8.5) * mm});
            skLineSegment(sketch, "E261.4.0.7", {"start": v(263.61, -8.5) * mm, "end": v(261.84, -5.42) * mm});
            skLineSegment(sketch, "E261.5.0.0", {"start": v(260.27, 8.46) * mm, "end": v(250.1, 2.58) * mm});
            skLineSegment(sketch, "E261.5.0.1", {"start": v(262.04, 5.38) * mm, "end": v(260.27, 8.46) * mm});
            skLineSegment(sketch, "E261.5.0.2", {"start": v(251.87, -0.5) * mm, "end": v(262.04, 5.38) * mm});
            skLineSegment(sketch, "E261.5.0.3", {"start": v(250.1, 2.58) * mm, "end": v(251.87, -0.5) * mm});
            skLineSegment(sketch, "E261.5.0.4", {"start": v(246.41, 0.46) * mm, "end": v(248.19, -2.62) * mm});
            skLineSegment(sketch, "E261.5.0.5", {"start": v(236.24, -5.42) * mm, "end": v(246.41, 0.46) * mm});
            skLineSegment(sketch, "E261.5.0.6", {"start": v(248.19, -2.62) * mm, "end": v(238.01, -8.5) * mm});
            skLineSegment(sketch, "E261.5.0.7", {"start": v(238.01, -8.5) * mm, "end": v(236.24, -5.42) * mm});
            skLineSegment(sketch, "E261.6.0.0", {"start": v(234.67, 8.46) * mm, "end": v(224.5, 2.58) * mm});
            skLineSegment(sketch, "E261.6.0.1", {"start": v(236.44, 5.38) * mm, "end": v(234.67, 8.46) * mm});
            skLineSegment(sketch, "E261.6.0.2", {"start": v(226.27, -0.5) * mm, "end": v(236.44, 5.38) * mm});
            skLineSegment(sketch, "E261.6.0.3", {"start": v(224.5, 2.58) * mm, "end": v(226.27, -0.5) * mm});
            skLineSegment(sketch, "E261.6.0.4", {"start": v(220.81, 0.46) * mm, "end": v(222.59, -2.62) * mm});
            skLineSegment(sketch, "E261.6.0.5", {"start": v(210.64, -5.42) * mm, "end": v(220.81, 0.46) * mm});
            skLineSegment(sketch, "E261.6.0.6", {"start": v(222.59, -2.62) * mm, "end": v(212.41, -8.5) * mm});
            skLineSegment(sketch, "E261.6.0.7", {"start": v(212.41, -8.5) * mm, "end": v(210.64, -5.42) * mm});
            skLineSegment(sketch, "E261.7.0.0", {"start": v(209.07, 8.46) * mm, "end": v(198.9, 2.58) * mm});
            skLineSegment(sketch, "E261.7.0.1", {"start": v(210.84, 5.38) * mm, "end": v(209.07, 8.46) * mm});
            skLineSegment(sketch, "E261.7.0.2", {"start": v(200.67, -0.5) * mm, "end": v(210.84, 5.38) * mm});
            skLineSegment(sketch, "E261.7.0.3", {"start": v(198.9, 2.58) * mm, "end": v(200.67, -0.5) * mm});
            skLineSegment(sketch, "E261.7.0.4", {"start": v(195.21, 0.46) * mm, "end": v(196.99, -2.62) * mm});
            skLineSegment(sketch, "E261.7.0.5", {"start": v(185.04, -5.42) * mm, "end": v(195.21, 0.46) * mm});
            skLineSegment(sketch, "E261.7.0.6", {"start": v(196.99, -2.62) * mm, "end": v(186.81, -8.5) * mm});
            skLineSegment(sketch, "E261.7.0.7", {"start": v(186.81, -8.5) * mm, "end": v(185.04, -5.42) * mm});
            skLineSegment(sketch, "E261.8.0.0", {"start": v(183.47, 8.46) * mm, "end": v(173.3, 2.58) * mm});
            skLineSegment(sketch, "E261.8.0.1", {"start": v(185.24, 5.38) * mm, "end": v(183.47, 8.46) * mm});
            skLineSegment(sketch, "E261.8.0.2", {"start": v(175.07, -0.5) * mm, "end": v(185.24, 5.38) * mm});
            skLineSegment(sketch, "E261.8.0.3", {"start": v(173.3, 2.58) * mm, "end": v(175.07, -0.5) * mm});
            skLineSegment(sketch, "E261.8.0.4", {"start": v(169.61, 0.46) * mm, "end": v(171.39, -2.62) * mm});
            skLineSegment(sketch, "E261.8.0.5", {"start": v(159.44, -5.42) * mm, "end": v(169.61, 0.46) * mm});
            skLineSegment(sketch, "E261.8.0.6", {"start": v(171.39, -2.62) * mm, "end": v(161.21, -8.5) * mm});
            skLineSegment(sketch, "E261.8.0.7", {"start": v(161.21, -8.5) * mm, "end": v(159.44, -5.42) * mm});
            skLineSegment(sketch, "E261.9.0.0", {"start": v(157.87, 8.46) * mm, "end": v(147.7, 2.58) * mm});
            skLineSegment(sketch, "E261.9.0.1", {"start": v(159.64, 5.38) * mm, "end": v(157.87, 8.46) * mm});
            skLineSegment(sketch, "E261.9.0.2", {"start": v(149.47, -0.5) * mm, "end": v(159.64, 5.38) * mm});
            skLineSegment(sketch, "E261.9.0.3", {"start": v(147.7, 2.58) * mm, "end": v(149.47, -0.5) * mm});
            skLineSegment(sketch, "E261.9.0.4", {"start": v(144.01, 0.46) * mm, "end": v(145.79, -2.62) * mm});
            skLineSegment(sketch, "E261.9.0.5", {"start": v(133.84, -5.42) * mm, "end": v(144.01, 0.46) * mm});
            skLineSegment(sketch, "E261.9.0.6", {"start": v(145.79, -2.62) * mm, "end": v(135.61, -8.5) * mm});
            skLineSegment(sketch, "E261.9.0.7", {"start": v(135.61, -8.5) * mm, "end": v(133.84, -5.42) * mm});
            skLineSegment(sketch, "E261.10.0.0", {"start": v(132.27, 8.46) * mm, "end": v(122.1, 2.58) * mm});
            skLineSegment(sketch, "E261.10.0.1", {"start": v(134.04, 5.38) * mm, "end": v(132.27, 8.46) * mm});
            skLineSegment(sketch, "E261.10.0.2", {"start": v(123.87, -0.5) * mm, "end": v(134.04, 5.38) * mm});
            skLineSegment(sketch, "E261.10.0.3", {"start": v(122.1, 2.58) * mm, "end": v(123.87, -0.5) * mm});
            skLineSegment(sketch, "E261.10.0.4", {"start": v(118.41, 0.46) * mm, "end": v(120.19, -2.62) * mm});
            skLineSegment(sketch, "E261.10.0.5", {"start": v(108.24, -5.42) * mm, "end": v(118.41, 0.46) * mm});
            skLineSegment(sketch, "E261.10.0.6", {"start": v(120.19, -2.62) * mm, "end": v(110.01, -8.5) * mm});
            skLineSegment(sketch, "E261.10.0.7", {"start": v(110.01, -8.5) * mm, "end": v(108.24, -5.42) * mm});
            skLineSegment(sketch, "E261.11.0.0", {"start": v(106.67, 8.46) * mm, "end": v(96.5, 2.58) * mm});
            skLineSegment(sketch, "E261.11.0.1", {"start": v(108.44, 5.38) * mm, "end": v(106.67, 8.46) * mm});
            skLineSegment(sketch, "E261.11.0.2", {"start": v(98.27, -0.5) * mm, "end": v(108.44, 5.38) * mm});
            skLineSegment(sketch, "E261.11.0.3", {"start": v(96.5, 2.58) * mm, "end": v(98.27, -0.5) * mm});
            skLineSegment(sketch, "E261.11.0.4", {"start": v(92.81, 0.46) * mm, "end": v(94.59, -2.62) * mm});
            skLineSegment(sketch, "E261.11.0.5", {"start": v(82.64, -5.42) * mm, "end": v(92.81, 0.46) * mm});
            skLineSegment(sketch, "E261.11.0.6", {"start": v(94.59, -2.62) * mm, "end": v(84.41, -8.5) * mm});
            skLineSegment(sketch, "E261.11.0.7", {"start": v(84.41, -8.5) * mm, "end": v(82.64, -5.42) * mm});
            skLineSegment(sketch, "E261.12.0.0", {"start": v(81.07, 8.46) * mm, "end": v(70.9, 2.58) * mm});
            skLineSegment(sketch, "E261.12.0.1", {"start": v(82.84, 5.38) * mm, "end": v(81.07, 8.46) * mm});
            skLineSegment(sketch, "E261.12.0.2", {"start": v(72.67, -0.5) * mm, "end": v(82.84, 5.38) * mm});
            skLineSegment(sketch, "E261.12.0.3", {"start": v(70.9, 2.58) * mm, "end": v(72.67, -0.5) * mm});
            skLineSegment(sketch, "E261.12.0.4", {"start": v(67.21, 0.46) * mm, "end": v(68.99, -2.62) * mm});
            skLineSegment(sketch, "E261.12.0.5", {"start": v(57.04, -5.42) * mm, "end": v(67.21, 0.46) * mm});
            skLineSegment(sketch, "E261.12.0.6", {"start": v(68.99, -2.62) * mm, "end": v(58.81, -8.5) * mm});
            skLineSegment(sketch, "E261.12.0.7", {"start": v(58.81, -8.5) * mm, "end": v(57.04, -5.42) * mm});
            skLineSegment(sketch, "E261.13.0.0", {"start": v(55.47, 8.46) * mm, "end": v(45.3, 2.58) * mm});
            skLineSegment(sketch, "E261.13.0.1", {"start": v(57.24, 5.38) * mm, "end": v(55.47, 8.46) * mm});
            skLineSegment(sketch, "E261.13.0.2", {"start": v(47.07, -0.5) * mm, "end": v(57.24, 5.38) * mm});
            skLineSegment(sketch, "E261.13.0.3", {"start": v(45.3, 2.58) * mm, "end": v(47.07, -0.5) * mm});
            skLineSegment(sketch, "E261.13.0.4", {"start": v(41.61, 0.46) * mm, "end": v(43.39, -2.62) * mm});
            skLineSegment(sketch, "E261.13.0.5", {"start": v(31.44, -5.42) * mm, "end": v(41.61, 0.46) * mm});
            skLineSegment(sketch, "E261.13.0.6", {"start": v(43.39, -2.62) * mm, "end": v(33.21, -8.5) * mm});
            skLineSegment(sketch, "E261.13.0.7", {"start": v(33.21, -8.5) * mm, "end": v(31.44, -5.42) * mm});
            skLineSegment(sketch, "E261.14.0.0", {"start": v(29.87, 8.46) * mm, "end": v(19.7, 2.58) * mm});
            skLineSegment(sketch, "E261.14.0.1", {"start": v(31.64, 5.38) * mm, "end": v(29.87, 8.46) * mm});
            skLineSegment(sketch, "E261.14.0.2", {"start": v(21.47, -0.5) * mm, "end": v(31.64, 5.38) * mm});
            skLineSegment(sketch, "E261.14.0.3", {"start": v(19.7, 2.58) * mm, "end": v(21.47, -0.5) * mm});
            skLineSegment(sketch, "E261.14.0.4", {"start": v(16.01, 0.46) * mm, "end": v(17.79, -2.62) * mm});
            skLineSegment(sketch, "E261.14.0.5", {"start": v(5.84, -5.42) * mm, "end": v(16.01, 0.46) * mm});
            skLineSegment(sketch, "E261.14.0.6", {"start": v(17.79, -2.62) * mm, "end": v(7.61, -8.5) * mm});
            skLineSegment(sketch, "E261.14.0.7", {"start": v(7.61, -8.5) * mm, "end": v(5.84, -5.42) * mm});
            skLineSegment(sketch, "E261.15.0.0", {"start": v(4.27, 8.46) * mm, "end": v(-5.9, 2.58) * mm});
            skLineSegment(sketch, "E261.15.0.1", {"start": v(6.04, 5.38) * mm, "end": v(4.27, 8.46) * mm});
            skLineSegment(sketch, "E261.15.0.2", {"start": v(-4.13, -0.5) * mm, "end": v(6.04, 5.38) * mm});
            skLineSegment(sketch, "E261.15.0.3", {"start": v(-5.9, 2.58) * mm, "end": v(-4.13, -0.5) * mm});
            skLineSegment(sketch, "E261.15.0.4", {"start": v(-9.59, 0.46) * mm, "end": v(-7.81, -2.62) * mm});
            skLineSegment(sketch, "E261.15.0.5", {"start": v(-19.76, -5.42) * mm, "end": v(-9.59, 0.46) * mm});
            skLineSegment(sketch, "E261.15.0.6", {"start": v(-7.81, -2.62) * mm, "end": v(-17.99, -8.5) * mm});
            skLineSegment(sketch, "E261.15.0.7", {"start": v(-17.99, -8.5) * mm, "end": v(-19.76, -5.42) * mm});
            skLineSegment(sketch, "E261.16.0.0", {"start": v(-21.33, 8.46) * mm, "end": v(-31.5, 2.58) * mm});
            skLineSegment(sketch, "E261.16.0.1", {"start": v(-19.56, 5.38) * mm, "end": v(-21.33, 8.46) * mm});
            skLineSegment(sketch, "E261.16.0.2", {"start": v(-29.73, -0.5) * mm, "end": v(-19.56, 5.38) * mm});
            skLineSegment(sketch, "E261.16.0.3", {"start": v(-31.5, 2.58) * mm, "end": v(-29.73, -0.5) * mm});
            skLineSegment(sketch, "E261.16.0.4", {"start": v(-35.19, 0.46) * mm, "end": v(-33.41, -2.62) * mm});
            skLineSegment(sketch, "E261.16.0.5", {"start": v(-45.36, -5.42) * mm, "end": v(-35.19, 0.46) * mm});
            skLineSegment(sketch, "E261.16.0.6", {"start": v(-33.41, -2.62) * mm, "end": v(-43.59, -8.5) * mm});
            skLineSegment(sketch, "E261.16.0.7", {"start": v(-43.59, -8.5) * mm, "end": v(-45.36, -5.42) * mm});
            skLineSegment(sketch, "E261.17.0.0", {"start": v(-46.93, 8.46) * mm, "end": v(-57.1, 2.58) * mm});
            skLineSegment(sketch, "E261.17.0.1", {"start": v(-45.16, 5.38) * mm, "end": v(-46.93, 8.46) * mm});
            skLineSegment(sketch, "E261.17.0.2", {"start": v(-55.33, -0.5) * mm, "end": v(-45.16, 5.38) * mm});
            skLineSegment(sketch, "E261.17.0.3", {"start": v(-57.1, 2.58) * mm, "end": v(-55.33, -0.5) * mm});
            skLineSegment(sketch, "E261.17.0.4", {"start": v(-60.79, 0.46) * mm, "end": v(-59.01, -2.62) * mm});
            skLineSegment(sketch, "E261.17.0.5", {"start": v(-70.96, -5.42) * mm, "end": v(-60.79, 0.46) * mm});
            skLineSegment(sketch, "E261.17.0.6", {"start": v(-59.01, -2.62) * mm, "end": v(-69.19, -8.5) * mm});
            skLineSegment(sketch, "E261.17.0.7", {"start": v(-69.19, -8.5) * mm, "end": v(-70.96, -5.42) * mm});
            skLineSegment(sketch, "E261.18.0.0", {"start": v(-72.53, 8.46) * mm, "end": v(-82.7, 2.58) * mm});
            skLineSegment(sketch, "E261.18.0.1", {"start": v(-70.76, 5.38) * mm, "end": v(-72.53, 8.46) * mm});
            skLineSegment(sketch, "E261.18.0.2", {"start": v(-80.93, -0.5) * mm, "end": v(-70.76, 5.38) * mm});
            skLineSegment(sketch, "E261.18.0.3", {"start": v(-82.7, 2.58) * mm, "end": v(-80.93, -0.5) * mm});
            skLineSegment(sketch, "E261.18.0.4", {"start": v(-86.39, 0.46) * mm, "end": v(-84.61, -2.62) * mm});
            skLineSegment(sketch, "E261.18.0.5", {"start": v(-96.56, -5.42) * mm, "end": v(-86.39, 0.46) * mm});
            skLineSegment(sketch, "E261.18.0.6", {"start": v(-84.61, -2.62) * mm, "end": v(-94.79, -8.5) * mm});
            skLineSegment(sketch, "E261.18.0.7", {"start": v(-94.79, -8.5) * mm, "end": v(-96.56, -5.42) * mm});
            skLineSegment(sketch, "E261.19.0.0", {"start": v(-98.13, 8.46) * mm, "end": v(-108.3, 2.58) * mm});
            skLineSegment(sketch, "E261.19.0.1", {"start": v(-96.36, 5.38) * mm, "end": v(-98.13, 8.46) * mm});
            skLineSegment(sketch, "E261.19.0.2", {"start": v(-106.53, -0.5) * mm, "end": v(-96.36, 5.38) * mm});
            skLineSegment(sketch, "E261.19.0.3", {"start": v(-108.3, 2.58) * mm, "end": v(-106.53, -0.5) * mm});
            skLineSegment(sketch, "E261.19.0.4", {"start": v(-111.99, 0.46) * mm, "end": v(-110.21, -2.62) * mm});
            skLineSegment(sketch, "E261.19.0.5", {"start": v(-122.16, -5.42) * mm, "end": v(-111.99, 0.46) * mm});
            skLineSegment(sketch, "E261.19.0.6", {"start": v(-110.21, -2.62) * mm, "end": v(-120.39, -8.5) * mm});
            skLineSegment(sketch, "E261.19.0.7", {"start": v(-120.39, -8.5) * mm, "end": v(-122.16, -5.42) * mm});
            skLineSegment(sketch, "E261.20.0.0", {"start": v(-123.73, 8.46) * mm, "end": v(-133.9, 2.58) * mm});
            skLineSegment(sketch, "E261.20.0.1", {"start": v(-121.96, 5.38) * mm, "end": v(-123.73, 8.46) * mm});
            skLineSegment(sketch, "E261.20.0.2", {"start": v(-132.13, -0.5) * mm, "end": v(-121.96, 5.38) * mm});
            skLineSegment(sketch, "E261.20.0.3", {"start": v(-133.9, 2.58) * mm, "end": v(-132.13, -0.5) * mm});
            skLineSegment(sketch, "E261.20.0.4", {"start": v(-137.59, 0.46) * mm, "end": v(-135.81, -2.62) * mm});
            skLineSegment(sketch, "E261.20.0.5", {"start": v(-147.76, -5.42) * mm, "end": v(-137.59, 0.46) * mm});
            skLineSegment(sketch, "E261.20.0.6", {"start": v(-135.81, -2.62) * mm, "end": v(-145.99, -8.5) * mm});
            skLineSegment(sketch, "E261.20.0.7", {"start": v(-145.99, -8.5) * mm, "end": v(-147.76, -5.42) * mm});
            skLineSegment(sketch, "E261.21.0.0", {"start": v(-149.33, 8.46) * mm, "end": v(-159.5, 2.58) * mm});
            skLineSegment(sketch, "E261.21.0.1", {"start": v(-147.56, 5.38) * mm, "end": v(-149.33, 8.46) * mm});
            skLineSegment(sketch, "E261.21.0.2", {"start": v(-157.73, -0.5) * mm, "end": v(-147.56, 5.38) * mm});
            skLineSegment(sketch, "E261.21.0.3", {"start": v(-159.5, 2.58) * mm, "end": v(-157.73, -0.5) * mm});
            skLineSegment(sketch, "E261.21.0.4", {"start": v(-163.19, 0.46) * mm, "end": v(-161.41, -2.62) * mm});
            skLineSegment(sketch, "E261.21.0.5", {"start": v(-173.36, -5.42) * mm, "end": v(-163.19, 0.46) * mm});
            skLineSegment(sketch, "E261.21.0.6", {"start": v(-161.41, -2.62) * mm, "end": v(-171.59, -8.5) * mm});
            skLineSegment(sketch, "E261.21.0.7", {"start": v(-171.59, -8.5) * mm, "end": v(-173.36, -5.42) * mm});
            skLineSegment(sketch, "E261.22.0.0", {"start": v(-174.93, 8.46) * mm, "end": v(-185.1, 2.58) * mm});
            skLineSegment(sketch, "E261.22.0.1", {"start": v(-173.16, 5.38) * mm, "end": v(-174.93, 8.46) * mm});
            skLineSegment(sketch, "E261.22.0.2", {"start": v(-183.33, -0.5) * mm, "end": v(-173.16, 5.38) * mm});
            skLineSegment(sketch, "E261.22.0.3", {"start": v(-185.1, 2.58) * mm, "end": v(-183.33, -0.5) * mm});
            skLineSegment(sketch, "E261.22.0.4", {"start": v(-188.79, 0.46) * mm, "end": v(-187.01, -2.62) * mm});
            skLineSegment(sketch, "E261.22.0.5", {"start": v(-198.96, -5.42) * mm, "end": v(-188.79, 0.46) * mm});
            skLineSegment(sketch, "E261.22.0.6", {"start": v(-187.01, -2.62) * mm, "end": v(-197.19, -8.5) * mm});
            skLineSegment(sketch, "E261.22.0.7", {"start": v(-197.19, -8.5) * mm, "end": v(-198.96, -5.42) * mm});
            skLineSegment(sketch, "E261.23.0.0", {"start": v(-200.53, 8.46) * mm, "end": v(-210.7, 2.58) * mm});
            skLineSegment(sketch, "E261.23.0.1", {"start": v(-198.76, 5.38) * mm, "end": v(-200.53, 8.46) * mm});
            skLineSegment(sketch, "E261.23.0.2", {"start": v(-208.93, -0.5) * mm, "end": v(-198.76, 5.38) * mm});
            skLineSegment(sketch, "E261.23.0.3", {"start": v(-210.7, 2.58) * mm, "end": v(-208.93, -0.5) * mm});
            skLineSegment(sketch, "E261.23.0.4", {"start": v(-214.39, 0.46) * mm, "end": v(-212.61, -2.62) * mm});
            skLineSegment(sketch, "E261.23.0.5", {"start": v(-224.56, -5.42) * mm, "end": v(-214.39, 0.46) * mm});
            skLineSegment(sketch, "E261.23.0.6", {"start": v(-212.61, -2.62) * mm, "end": v(-222.79, -8.5) * mm});
            skLineSegment(sketch, "E261.23.0.7", {"start": v(-222.79, -8.5) * mm, "end": v(-224.56, -5.42) * mm});
            skLineSegment(sketch, "E261.24.0.0", {"start": v(-226.13, 8.46) * mm, "end": v(-236.3, 2.58) * mm});
            skLineSegment(sketch, "E261.24.0.1", {"start": v(-224.36, 5.38) * mm, "end": v(-226.13, 8.46) * mm});
            skLineSegment(sketch, "E261.24.0.2", {"start": v(-234.53, -0.5) * mm, "end": v(-224.36, 5.38) * mm});
            skLineSegment(sketch, "E261.24.0.3", {"start": v(-236.3, 2.58) * mm, "end": v(-234.53, -0.5) * mm});
            skLineSegment(sketch, "E261.24.0.4", {"start": v(-239.99, 0.46) * mm, "end": v(-238.21, -2.62) * mm});
            skLineSegment(sketch, "E261.24.0.5", {"start": v(-250.16, -5.42) * mm, "end": v(-239.99, 0.46) * mm});
            skLineSegment(sketch, "E261.24.0.6", {"start": v(-238.21, -2.62) * mm, "end": v(-248.39, -8.5) * mm});
            skLineSegment(sketch, "E261.24.0.7", {"start": v(-248.39, -8.5) * mm, "end": v(-250.16, -5.42) * mm});
            skLineSegment(sketch, "E261.25.0.0", {"start": v(-251.73, 8.46) * mm, "end": v(-261.9, 2.58) * mm});
            skLineSegment(sketch, "E261.25.0.1", {"start": v(-249.96, 5.38) * mm, "end": v(-251.73, 8.46) * mm});
            skLineSegment(sketch, "E261.25.0.2", {"start": v(-260.13, -0.5) * mm, "end": v(-249.96, 5.38) * mm});
            skLineSegment(sketch, "E261.25.0.3", {"start": v(-261.9, 2.58) * mm, "end": v(-260.13, -0.5) * mm});
            skLineSegment(sketch, "E261.25.0.4", {"start": v(-265.59, 0.46) * mm, "end": v(-263.81, -2.62) * mm});
            skLineSegment(sketch, "E261.25.0.5", {"start": v(-275.76, -5.42) * mm, "end": v(-265.59, 0.46) * mm});
            skLineSegment(sketch, "E261.25.0.6", {"start": v(-263.81, -2.62) * mm, "end": v(-273.99, -8.5) * mm});
            skLineSegment(sketch, "E261.25.0.7", {"start": v(-273.99, -8.5) * mm, "end": v(-275.76, -5.42) * mm});
            skLineSegment(sketch, "E261.26.0.0", {"start": v(-277.33, 8.46) * mm, "end": v(-287.5, 2.58) * mm});
            skLineSegment(sketch, "E261.26.0.1", {"start": v(-275.56, 5.38) * mm, "end": v(-277.33, 8.46) * mm});
            skLineSegment(sketch, "E261.26.0.2", {"start": v(-285.73, -0.5) * mm, "end": v(-275.56, 5.38) * mm});
            skLineSegment(sketch, "E261.26.0.3", {"start": v(-287.5, 2.58) * mm, "end": v(-285.73, -0.5) * mm});
            skLineSegment(sketch, "E261.26.0.4", {"start": v(-291.19, 0.46) * mm, "end": v(-289.41, -2.62) * mm});
            skLineSegment(sketch, "E261.26.0.5", {"start": v(-301.36, -5.42) * mm, "end": v(-291.19, 0.46) * mm});
            skLineSegment(sketch, "E261.26.0.6", {"start": v(-289.41, -2.62) * mm, "end": v(-299.59, -8.5) * mm});
            skLineSegment(sketch, "E261.26.0.7", {"start": v(-299.59, -8.5) * mm, "end": v(-301.36, -5.42) * mm});
            skLineSegment(sketch, "E261.27.0.0", {"start": v(-302.93, 8.46) * mm, "end": v(-313.1, 2.58) * mm});
            skLineSegment(sketch, "E261.27.0.1", {"start": v(-301.16, 5.38) * mm, "end": v(-302.93, 8.46) * mm});
            skLineSegment(sketch, "E261.27.0.2", {"start": v(-311.33, -0.5) * mm, "end": v(-301.16, 5.38) * mm});
            skLineSegment(sketch, "E261.27.0.3", {"start": v(-313.1, 2.58) * mm, "end": v(-311.33, -0.5) * mm});
            skLineSegment(sketch, "E261.27.0.4", {"start": v(-316.79, 0.46) * mm, "end": v(-315.01, -2.62) * mm});
            skLineSegment(sketch, "E261.27.0.5", {"start": v(-326.96, -5.42) * mm, "end": v(-316.79, 0.46) * mm});
            skLineSegment(sketch, "E261.27.0.6", {"start": v(-315.01, -2.62) * mm, "end": v(-325.19, -8.5) * mm});
            skLineSegment(sketch, "E261.27.0.7", {"start": v(-325.19, -8.5) * mm, "end": v(-326.96, -5.42) * mm});
            skLineSegment(sketch, "E261.28.0.0", {"start": v(-328.53, 8.46) * mm, "end": v(-338.7, 2.58) * mm});
            skLineSegment(sketch, "E261.28.0.1", {"start": v(-326.76, 5.38) * mm, "end": v(-328.53, 8.46) * mm});
            skLineSegment(sketch, "E261.28.0.2", {"start": v(-336.93, -0.5) * mm, "end": v(-326.76, 5.38) * mm});
            skLineSegment(sketch, "E261.28.0.3", {"start": v(-338.7, 2.58) * mm, "end": v(-336.93, -0.5) * mm});
            skLineSegment(sketch, "E261.28.0.4", {"start": v(-342.39, 0.46) * mm, "end": v(-340.61, -2.62) * mm});
            skLineSegment(sketch, "E261.28.0.5", {"start": v(-352.56, -5.42) * mm, "end": v(-342.39, 0.46) * mm});
            skLineSegment(sketch, "E261.28.0.6", {"start": v(-340.61, -2.62) * mm, "end": v(-350.79, -8.5) * mm});
            skLineSegment(sketch, "E261.28.0.7", {"start": v(-350.79, -8.5) * mm, "end": v(-352.56, -5.42) * mm});
            skLineSegment(sketch, "E261.29.0.0", {"start": v(-354.13, 8.46) * mm, "end": v(-364.3, 2.58) * mm});
            skLineSegment(sketch, "E261.29.0.1", {"start": v(-352.36, 5.38) * mm, "end": v(-354.13, 8.46) * mm});
            skLineSegment(sketch, "E261.29.0.2", {"start": v(-362.53, -0.5) * mm, "end": v(-352.36, 5.38) * mm});
            skLineSegment(sketch, "E261.29.0.3", {"start": v(-364.3, 2.58) * mm, "end": v(-362.53, -0.5) * mm});
            skLineSegment(sketch, "E261.29.0.4", {"start": v(-367.99, 0.46) * mm, "end": v(-366.21, -2.62) * mm});
            skLineSegment(sketch, "E261.29.0.5", {"start": v(-378.16, -5.42) * mm, "end": v(-367.99, 0.46) * mm});
            skLineSegment(sketch, "E261.29.0.6", {"start": v(-366.21, -2.62) * mm, "end": v(-376.39, -8.5) * mm});
            skLineSegment(sketch, "E261.29.0.7", {"start": v(-376.39, -8.5) * mm, "end": v(-378.16, -5.42) * mm});
            skLineSegment(sketch, "E261.30.0.0", {"start": v(-379.73, 8.46) * mm, "end": v(-389.9, 2.58) * mm});
            skLineSegment(sketch, "E261.30.0.1", {"start": v(-377.96, 5.38) * mm, "end": v(-379.73, 8.46) * mm});
            skLineSegment(sketch, "E261.30.0.2", {"start": v(-388.13, -0.5) * mm, "end": v(-377.96, 5.38) * mm});
            skLineSegment(sketch, "E261.30.0.3", {"start": v(-389.9, 2.58) * mm, "end": v(-388.13, -0.5) * mm});
            skLineSegment(sketch, "E261.direction1", {"start": v(378.1, 2.58) * mm, "end": v(352.5, 2.58) * mm, "construction": true});
            skCircle(sketch, "E262", {"center": v(-392, -6.3) * mm, "radius": 2.93 * mm});
            skCircle(sketch, "E263", {"center": v(392, -6.3) * mm, "radius": 2.93 * mm});
            skLineSegment(sketch, "E264.bottom", {"start": v(400, -12.5) * mm, "end": v(-400, -12.5) * mm});
            skLineSegment(sketch, "E264.top", {"start": v(400, 12.5) * mm, "end": v(-400, 12.5) * mm});
            skLineSegment(sketch, "E264.left", {"start": v(400, -12.5) * mm, "end": v(400, 12.5) * mm});
            skLineSegment(sketch, "E264.right", {"start": v(-400, -12.5) * mm, "end": v(-400, 12.5) * mm});
            skSolve(sketch);
        }
        {
            var Q0;
            Q0 = qSketchRegion(id + "F1", true);
            extrude(context, id + "F2", {"entities" : qUnion([Q0]), "depth" : 5 * mm, "offsetDistance" : 25 * mm});
        }
    });
